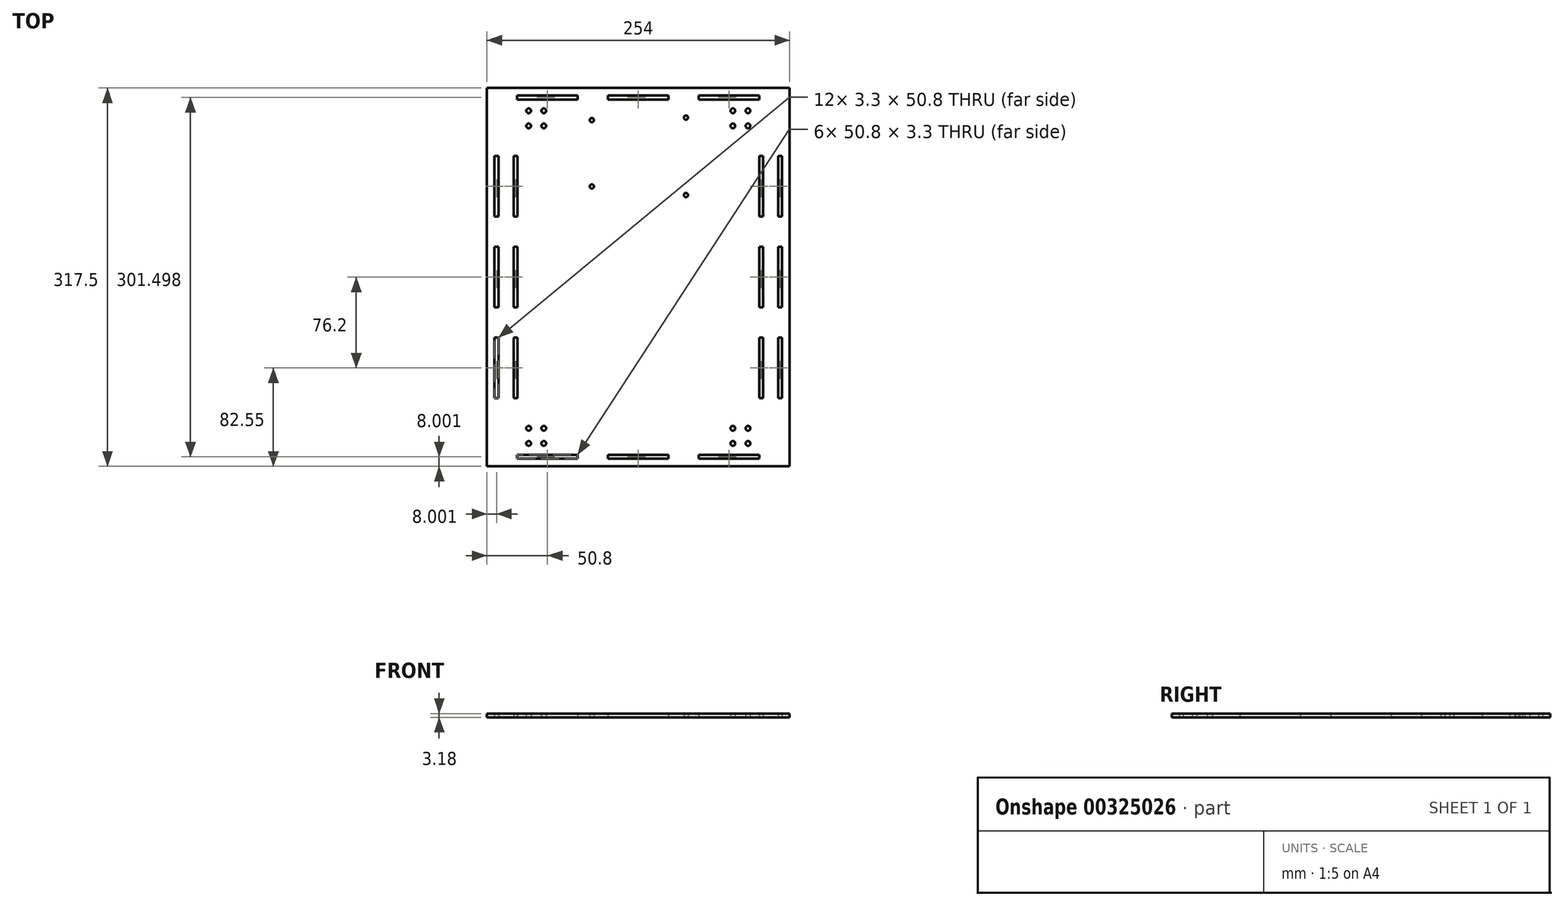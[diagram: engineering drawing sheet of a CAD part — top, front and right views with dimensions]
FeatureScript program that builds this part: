
annotation { "Feature Type Name" : "Feature", "Feature Type Description" : "" }
export const myFeature = defineFeature(function(context is Context, id is Id, definition is map)
    precondition{}
    {
        {
            var Q0;
            Q0=qCreatedBy(makeId("Top.planeOp"),FACE);
            var sketch = newSketch(context, id + "F0", { "sketchPlane" : qUnion([Q0])});
            skLineSegment(sketch, "E0.bottom", {"start": v(127, -158.75) * mm, "end": v(-127, -158.75) * mm});
            skLineSegment(sketch, "E0.top", {"start": v(127, 158.75) * mm, "end": v(-127, 158.75) * mm});
            skLineSegment(sketch, "E0.left", {"start": v(127, -158.75) * mm, "end": v(127, 158.75) * mm});
            skLineSegment(sketch, "E0.right", {"start": v(-127, -158.75) * mm, "end": v(-127, 158.75) * mm});
            skPoint(sketch, "E0.middle", {"position": v(0, 0) * mm});
            skLineSegment(sketch, "E1.bottom", {"start": v(-101.6, 152.4) * mm, "end": v(-50.8, 152.4) * mm});
            skLineSegment(sketch, "E1.top", {"start": v(-101.6, 149.1) * mm, "end": v(-50.8, 149.1) * mm});
            skLineSegment(sketch, "E1.left", {"start": v(-101.6, 152.4) * mm, "end": v(-101.6, 149.1) * mm});
            skLineSegment(sketch, "E1.right", {"start": v(-50.8, 152.4) * mm, "end": v(-50.8, 149.1) * mm});
            skLineSegment(sketch, "E2.bottom", {"start": v(-25.4, 152.4) * mm, "end": v(25.4, 152.4) * mm});
            skLineSegment(sketch, "E2.top", {"start": v(-25.4, 149.1) * mm, "end": v(25.4, 149.1) * mm});
            skLineSegment(sketch, "E2.left", {"start": v(-25.4, 152.4) * mm, "end": v(-25.4, 149.1) * mm});
            skLineSegment(sketch, "E2.right", {"start": v(25.4, 152.4) * mm, "end": v(25.4, 149.1) * mm});
            skLineSegment(sketch, "E3", {"start": v(-50.8, 152.4) * mm, "end": v(-25.4, 152.4) * mm, "construction": true});
            skLineSegment(sketch, "E4", {"start": v(-101.6, 152.4) * mm, "end": v(-127, 152.4) * mm, "construction": true});
            skLineSegment(sketch, "E5.MirrorCS", {"start": v(101.6, 149.1) * mm, "end": v(50.8, 149.1) * mm});
            skLineSegment(sketch, "E6.MirrorCS", {"start": v(101.6, 152.4) * mm, "end": v(50.8, 152.4) * mm});
            skLineSegment(sketch, "E7.MirrorCS", {"start": v(50.8, 152.4) * mm, "end": v(50.8, 149.1) * mm});
            skLineSegment(sketch, "E8.MirrorCS", {"start": v(101.6, 152.4) * mm, "end": v(101.6, 149.1) * mm});
            skLineSegment(sketch, "E9.MirrorCS", {"start": v(-50.8, -152.4) * mm, "end": v(-50.8, -149.1) * mm});
            skLineSegment(sketch, "E10.MirrorCS", {"start": v(-25.4, -149.1) * mm, "end": v(25.4, -149.1) * mm});
            skLineSegment(sketch, "E11.MirrorCS", {"start": v(25.4, -152.4) * mm, "end": v(25.4, -149.1) * mm});
            skLineSegment(sketch, "E12.MirrorCS", {"start": v(101.6, -149.1) * mm, "end": v(50.8, -149.1) * mm});
            skLineSegment(sketch, "E13.MirrorCS", {"start": v(50.8, -152.4) * mm, "end": v(50.8, -149.1) * mm});
            skLineSegment(sketch, "E14.MirrorCS", {"start": v(-101.6, -149.1) * mm, "end": v(-50.8, -149.1) * mm});
            skLineSegment(sketch, "E15.MirrorCS", {"start": v(101.6, -152.4) * mm, "end": v(101.6, -149.1) * mm});
            skLineSegment(sketch, "E16.MirrorCS", {"start": v(-25.4, -152.4) * mm, "end": v(-25.4, -149.1) * mm});
            skLineSegment(sketch, "E17.MirrorCS", {"start": v(101.6, -152.4) * mm, "end": v(50.8, -152.4) * mm});
            skLineSegment(sketch, "E18.MirrorCS", {"start": v(-25.4, -152.4) * mm, "end": v(25.4, -152.4) * mm});
            skLineSegment(sketch, "E19.MirrorCS", {"start": v(-50.8, -152.4) * mm, "end": v(-25.4, -152.4) * mm, "construction": true});
            skLineSegment(sketch, "E20.MirrorCS", {"start": v(-101.6, -152.4) * mm, "end": v(-50.8, -152.4) * mm});
            skLineSegment(sketch, "E21.MirrorCS", {"start": v(-101.6, -152.4) * mm, "end": v(-101.6, -149.1) * mm});
            skLineSegment(sketch, "E22.bottom", {"start": v(-120.65, 101.6) * mm, "end": v(-117.35, 101.6) * mm});
            skLineSegment(sketch, "E22.top", {"start": v(-120.65, 50.8) * mm, "end": v(-117.35, 50.8) * mm});
            skLineSegment(sketch, "E22.left", {"start": v(-120.65, 101.6) * mm, "end": v(-120.65, 50.8) * mm});
            skLineSegment(sketch, "E22.right", {"start": v(-117.35, 101.6) * mm, "end": v(-117.35, 50.8) * mm});
            skLineSegment(sketch, "E23.0.1.0", {"start": v(-117.35, 25.4) * mm, "end": v(-117.35, -25.4) * mm});
            skLineSegment(sketch, "E23.0.1.1", {"start": v(-120.65, 25.4) * mm, "end": v(-120.65, -25.4) * mm});
            skLineSegment(sketch, "E23.0.1.2", {"start": v(-120.65, 25.4) * mm, "end": v(-117.35, 25.4) * mm});
            skLineSegment(sketch, "E23.0.1.3", {"start": v(-120.65, -25.4) * mm, "end": v(-117.35, -25.4) * mm});
            skLineSegment(sketch, "E23.0.2.0", {"start": v(-117.35, -50.8) * mm, "end": v(-117.35, -101.6) * mm});
            skLineSegment(sketch, "E23.0.2.1", {"start": v(-120.65, -50.8) * mm, "end": v(-120.65, -101.6) * mm});
            skLineSegment(sketch, "E23.0.2.2", {"start": v(-120.65, -50.8) * mm, "end": v(-117.35, -50.8) * mm});
            skLineSegment(sketch, "E23.0.2.3", {"start": v(-120.65, -101.6) * mm, "end": v(-117.35, -101.6) * mm});
            skLineSegment(sketch, "E23.direction1", {"start": v(-120.65, 50.8) * mm, "end": v(-104.65, 50.8) * mm, "construction": true});
            skLineSegment(sketch, "E23.direction2", {"start": v(-120.65, 50.8) * mm, "end": v(-120.65, -25.4) * mm, "construction": true});
            skLineSegment(sketch, "E24.MirrorCS", {"start": v(117.35, 25.4) * mm, "end": v(117.35, -25.4) * mm});
            skLineSegment(sketch, "E25.MirrorCS", {"start": v(120.65, -50.8) * mm, "end": v(117.35, -50.8) * mm});
            skLineSegment(sketch, "E26.MirrorCS", {"start": v(120.65, 25.4) * mm, "end": v(120.65, -25.4) * mm});
            skLineSegment(sketch, "E27.MirrorCS", {"start": v(120.65, -101.6) * mm, "end": v(117.35, -101.6) * mm});
            skLineSegment(sketch, "E28.MirrorCS", {"start": v(120.65, 25.4) * mm, "end": v(117.35, 25.4) * mm});
            skLineSegment(sketch, "E29.MirrorCS", {"start": v(120.65, -25.4) * mm, "end": v(117.35, -25.4) * mm});
            skLineSegment(sketch, "E30.MirrorCS", {"start": v(120.65, 50.8) * mm, "end": v(120.65, -25.4) * mm, "construction": true});
            skLineSegment(sketch, "E31.MirrorCS", {"start": v(120.65, 101.6) * mm, "end": v(117.35, 101.6) * mm});
            skLineSegment(sketch, "E32.MirrorCS", {"start": v(120.65, 50.8) * mm, "end": v(117.35, 50.8) * mm});
            skLineSegment(sketch, "E33.MirrorCS", {"start": v(120.65, 101.6) * mm, "end": v(120.65, 50.8) * mm});
            skLineSegment(sketch, "E34.MirrorCS", {"start": v(117.35, -50.8) * mm, "end": v(117.35, -101.6) * mm});
            skLineSegment(sketch, "E35.MirrorCS", {"start": v(117.35, 101.6) * mm, "end": v(117.35, 50.8) * mm});
            skLineSegment(sketch, "E36.MirrorCS", {"start": v(120.65, -50.8) * mm, "end": v(120.65, -101.6) * mm});
            skPoint(sketch, "E37.middle", {"position": v(0, 103.9) * mm});
            skCircle(sketch, "E38", {"center": v(39.92, 133.86) * mm, "radius": 1.75 * mm});
            skCircle(sketch, "E39", {"center": v(39.92, 68.86) * mm, "radius": 1.75 * mm});
            skCircle(sketch, "E40", {"center": v(-39.04, 76.04) * mm, "radius": 1.75 * mm});
            skCircle(sketch, "E41.MirrorC", {"center": v(-39.04, 131.78) * mm, "radius": 1.75 * mm});
            skLineSegment(sketch, "E42.0.1.0", {"start": v(-101.35, 101.6) * mm, "end": v(-101.35, 50.8) * mm});
            skLineSegment(sketch, "E42.3.1.0", {"start": v(-104.65, 101.6) * mm, "end": v(-104.65, 50.8) * mm});
            skLineSegment(sketch, "E42.6.1.0", {"start": v(-104.65, 101.6) * mm, "end": v(-101.35, 101.6) * mm});
            skLineSegment(sketch, "E42.9.1.0", {"start": v(-104.65, 50.8) * mm, "end": v(-101.35, 50.8) * mm});
            skLineSegment(sketch, "E42.0.1.1", {"start": v(-101.35, 25.4) * mm, "end": v(-101.35, -25.4) * mm});
            skLineSegment(sketch, "E42.3.1.1", {"start": v(-104.65, 25.4) * mm, "end": v(-104.65, -25.4) * mm});
            skLineSegment(sketch, "E42.6.1.1", {"start": v(-104.65, 25.4) * mm, "end": v(-101.35, 25.4) * mm});
            skLineSegment(sketch, "E42.9.1.1", {"start": v(-104.65, -25.4) * mm, "end": v(-101.35, -25.4) * mm});
            skLineSegment(sketch, "E42.0.1.2", {"start": v(-101.35, -50.8) * mm, "end": v(-101.35, -101.6) * mm});
            skLineSegment(sketch, "E42.3.1.2", {"start": v(-104.65, -50.8) * mm, "end": v(-104.65, -101.6) * mm});
            skLineSegment(sketch, "E42.6.1.2", {"start": v(-104.65, -50.8) * mm, "end": v(-101.35, -50.8) * mm});
            skLineSegment(sketch, "E42.9.1.2", {"start": v(-104.65, -101.6) * mm, "end": v(-101.35, -101.6) * mm});
            skLineSegment(sketch, "E43.MirrorCS", {"start": v(104.65, 101.6) * mm, "end": v(104.65, 50.8) * mm});
            skLineSegment(sketch, "E44.MirrorCS", {"start": v(104.65, 101.6) * mm, "end": v(101.35, 101.6) * mm});
            skLineSegment(sketch, "E45.MirrorCS", {"start": v(104.65, 50.8) * mm, "end": v(101.35, 50.8) * mm});
            skLineSegment(sketch, "E46.MirrorCS", {"start": v(104.65, -50.8) * mm, "end": v(104.65, -101.6) * mm});
            skLineSegment(sketch, "E47.MirrorCS", {"start": v(101.35, 25.4) * mm, "end": v(101.35, -25.4) * mm});
            skLineSegment(sketch, "E48.MirrorCS", {"start": v(104.65, -50.8) * mm, "end": v(101.35, -50.8) * mm});
            skLineSegment(sketch, "E49.MirrorCS", {"start": v(104.65, 25.4) * mm, "end": v(104.65, -25.4) * mm});
            skLineSegment(sketch, "E50.MirrorCS", {"start": v(104.65, -101.6) * mm, "end": v(101.35, -101.6) * mm});
            skLineSegment(sketch, "E51.MirrorCS", {"start": v(104.65, 25.4) * mm, "end": v(101.35, 25.4) * mm});
            skLineSegment(sketch, "E52.MirrorCS", {"start": v(104.65, -25.4) * mm, "end": v(101.35, -25.4) * mm});
            skLineSegment(sketch, "E53.MirrorCS", {"start": v(101.35, 101.6) * mm, "end": v(101.35, 50.8) * mm});
            skLineSegment(sketch, "E54.MirrorCS", {"start": v(101.35, -50.8) * mm, "end": v(101.35, -101.6) * mm});
            skLineSegment(sketch, "E55", {"start": v(-101.35, 101.6) * mm, "end": v(-101.6, 149.1) * mm, "construction": true});
            skCircle(sketch, "E56", {"center": v(-92.02, 139.57) * mm, "radius": 1.98 * mm});
            skCircle(sketch, "E57", {"center": v(-79.32, 139.57) * mm, "radius": 1.98 * mm});
            skCircle(sketch, "E58", {"center": v(-92.02, 126.87) * mm, "radius": 1.98 * mm});
            skCircle(sketch, "E59", {"center": v(-79.32, 126.87) * mm, "radius": 1.98 * mm});
            skCircle(sketch, "E60.MirrorC", {"center": v(92.02, 126.87) * mm, "radius": 1.98 * mm});
            skCircle(sketch, "E61.MirrorC", {"center": v(92.02, 139.57) * mm, "radius": 1.98 * mm});
            skCircle(sketch, "E62.MirrorC", {"center": v(79.32, 139.57) * mm, "radius": 1.98 * mm});
            skCircle(sketch, "E63.MirrorC", {"center": v(79.32, 126.87) * mm, "radius": 1.98 * mm});
            skCircle(sketch, "E64.MirrorC", {"center": v(-92.02, -139.57) * mm, "radius": 1.98 * mm});
            skCircle(sketch, "E65.MirrorC", {"center": v(-92.02, -126.87) * mm, "radius": 1.98 * mm});
            skCircle(sketch, "E66.MirrorC", {"center": v(-79.32, -139.57) * mm, "radius": 1.98 * mm});
            skCircle(sketch, "E67.MirrorC", {"center": v(-79.32, -126.87) * mm, "radius": 1.98 * mm});
            skCircle(sketch, "E68.MirrorC", {"center": v(79.32, -139.57) * mm, "radius": 1.98 * mm});
            skCircle(sketch, "E69.MirrorC", {"center": v(92.02, -126.87) * mm, "radius": 1.98 * mm});
            skCircle(sketch, "E70.MirrorC", {"center": v(79.32, -126.87) * mm, "radius": 1.98 * mm});
            skCircle(sketch, "E71.MirrorC", {"center": v(92.02, -139.57) * mm, "radius": 1.98 * mm});
            skSolve(sketch);
        }
        {
            var Q0;
            Q0=makeQuery(id+"F0.imprint","IMPRINT",FACE,{"disambiguationData":[TD([[makeQuery(id+"F0.imprint","IMPRINT",EDGE,{"derivedFrom":sQuery(id+"F0.wireOp",EDGE,"E0.bottom")}),-1.0]])]});
            extrude(context, id + "F1", {"entities" : qUnion([Q0]), "depth" : 3.17 * mm});
        }
    });
